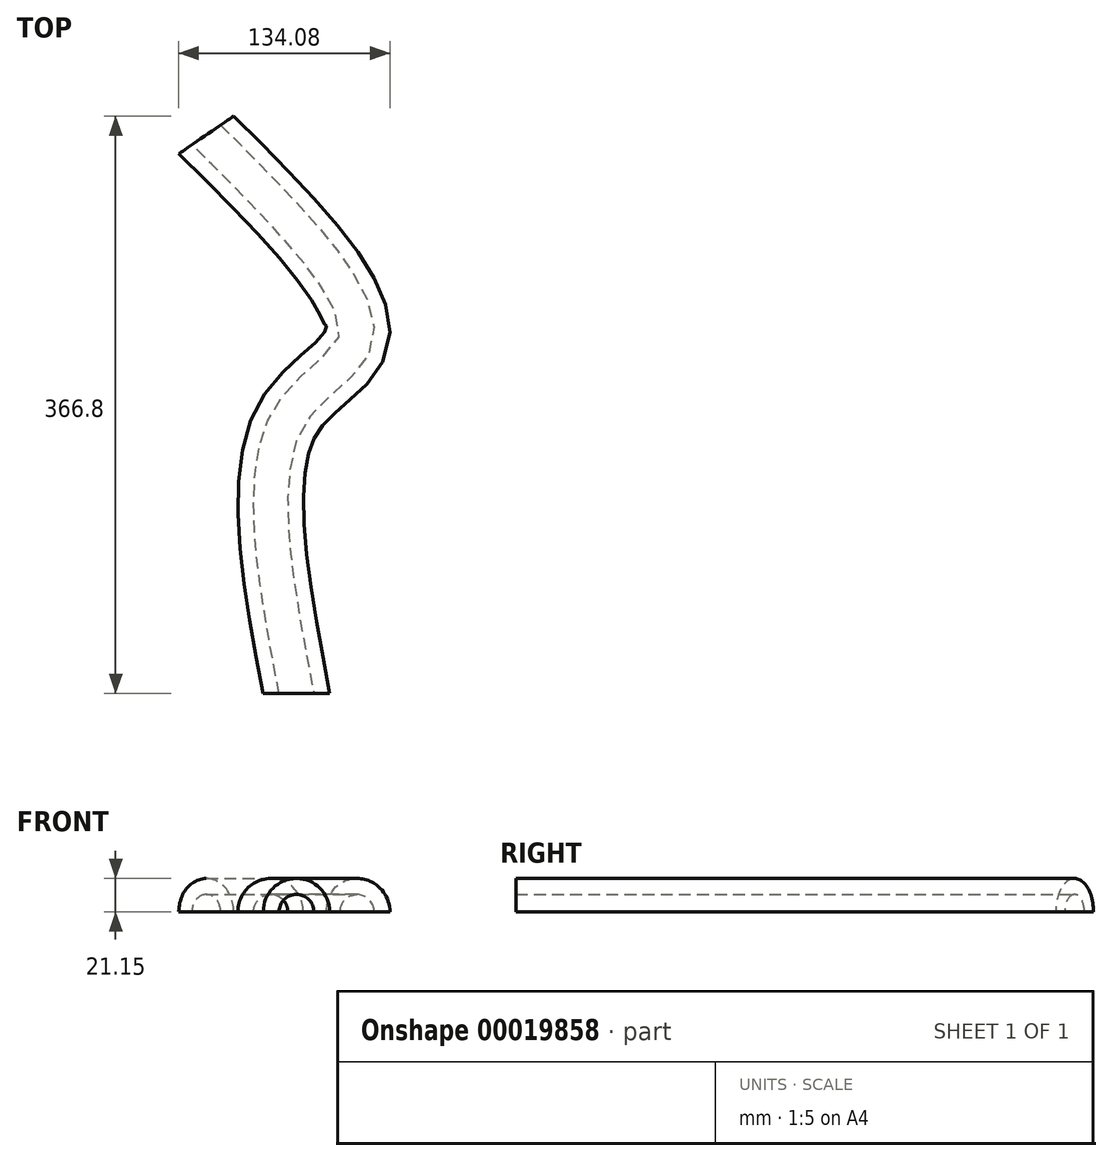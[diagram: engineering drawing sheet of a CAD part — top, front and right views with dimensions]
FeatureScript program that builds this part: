
annotation { "Feature Type Name" : "Feature", "Feature Type Description" : "" }
export const myFeature = defineFeature(function(context is Context, id is Id, definition is map)
    precondition{}
    {
        {
            var Q0;
            Q0=qCreatedBy(makeId("Top.planeOp"),FACE);
            var sketch = newSketch(context, id + "F0", { "sketchPlane" : qUnion([Q0])});
            skFitSpline(sketch, "E0", {"points": [v(-106.66, 105.3) * mm, v(-11.3, -23.46) * mm, v(-54.37, -74.43) * mm, v(-49.34, -249.7) * mm], "startDerivative": vector(405.98, -403.19) * mm, "endDerivative": vector(102.25, -535.93) * mm});
            skSolve(sketch);
        }
        {
            var Q0;
            Q0=qCreatedBy(makeId("Front.planeOp"),FACE);
            var Q1;
            Q1=sQuery(id+"F0.wireOp",VERTEX,"E0.end");
            cPlane(context, id + "F1", {"entities" : qUnion([Q0, Q1]), "cplaneType" : CPlaneType.PLANE_POINT, "offset" : 150 * mm, "width" : 150 * mm, "height" : 150 * mm});
        }
        {
            var Q0;
            Q0=qCreatedBy(id+"F1.planeOp",FACE);
            var sketch = newSketch(context, id + "F2", { "sketchPlane" : qUnion([Q0])});
            skLineSegment(sketch, "E1", {"start": v(-131.65, 0) * mm, "end": v(39.09, 0) * mm, "construction": true});
            skArc(sketch, "E2", {"start": v(-28.45, 0) * mm, "mid": v(-49.6, 21.15) * mm, "end": v(-70.76, 0) * mm});
            skLineSegment(sketch, "E3", {"start": v(-70.76, 0) * mm, "end": v(-28.45, 0) * mm});
            skSolve(sketch);
        }
        {
            var Q0;
            Q0=makeQuery(id+"F2.imprint","IMPRINT",FACE,{"disambiguationData":[TD([[makeQuery(id+"F2.imprint","IMPRINT",EDGE,{"derivedFrom":sQuery(id+"F2.wireOp",EDGE,"E2")}),1.0]])]});
            var Q1;
            Q1=sQuery(id+"F0.wireOp",EDGE,"E0");
            sweep(context, id + "F3", {"profiles" : qUnion([Q0]), "path" : qUnion([Q1])});
        }
        {
            var Q0;
            Q0=qCreatedBy(id+"F1.planeOp",FACE);
            var sketch = newSketch(context, id + "F4", { "sketchPlane" : qUnion([Q0])});
            skCircle(sketch, "E4", {"center": v(-49.6, 0) * mm, "radius": 11.02 * mm});
            skSolve(sketch);
        }
        {
            var Q0;
            Q0 = qSketchRegion(id + "F4", true);
            var Q1;
            Q1=sQuery(id+"F0.wireOp",EDGE,"E0");
            sweep(context, id + "F5", {"operationType" : NewBodyOperationType.REMOVE, "profiles" : qUnion([Q0]), "path" : qUnion([Q1])});
        }
    });
